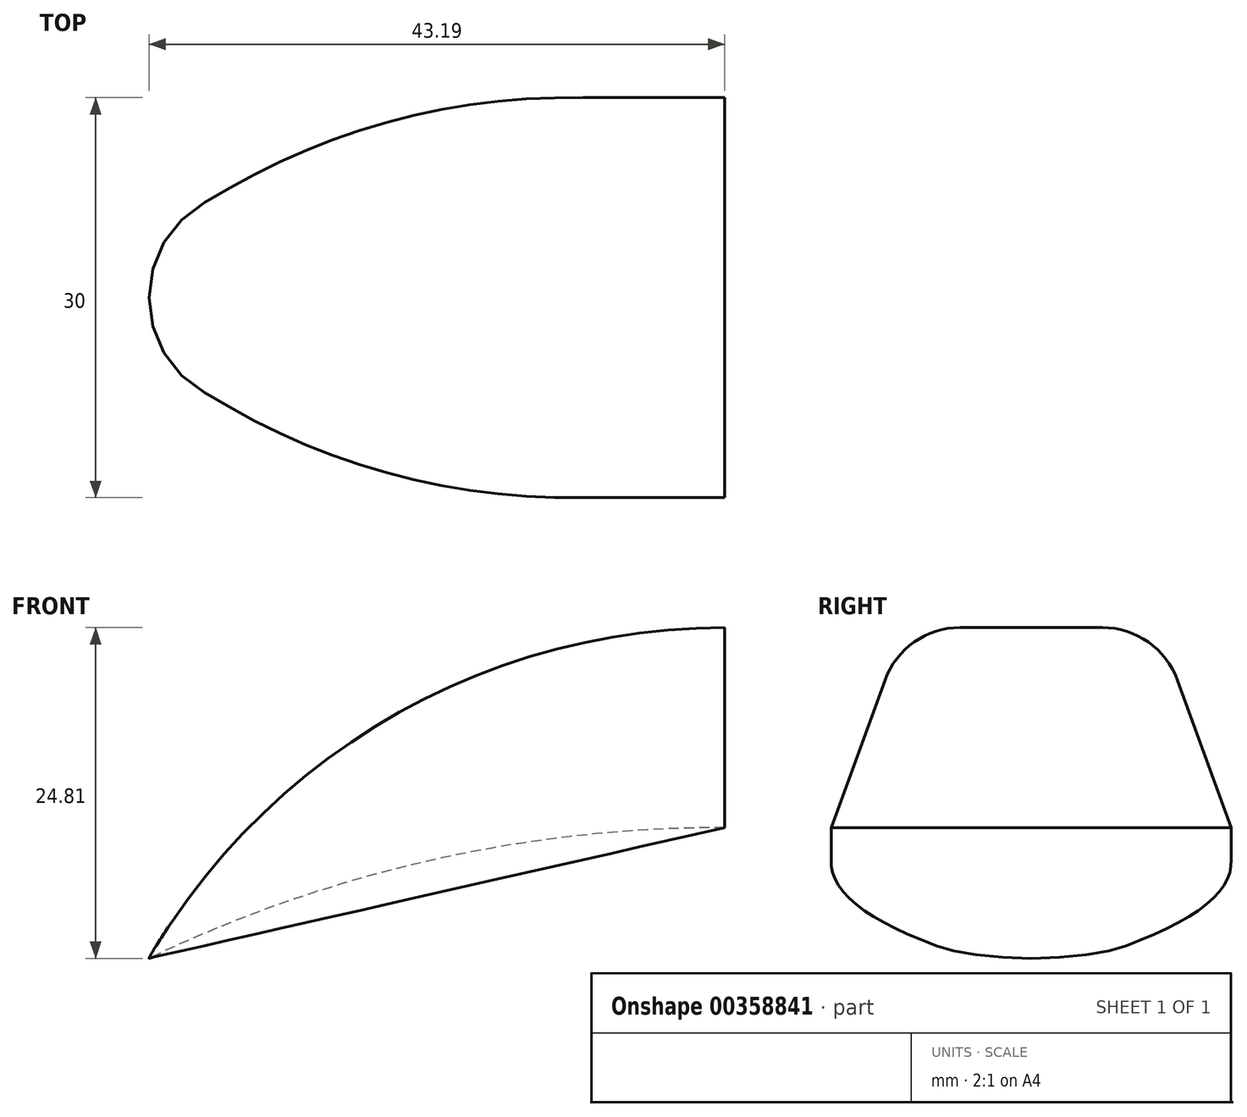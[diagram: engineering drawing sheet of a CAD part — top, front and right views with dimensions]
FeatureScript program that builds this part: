
annotation { "Feature Type Name" : "Feature", "Feature Type Description" : "" }
export const myFeature = defineFeature(function(context is Context, id is Id, definition is map)
    precondition{}
    {
        {
            var Q0;
            Q0=qCreatedBy(makeId("Right.planeOp"),FACE);
            var sketch = newSketch(context, id + "F0", { "sketchPlane" : qUnion([Q0])});
            skLineSegment(sketch, "E0", {"start": v(10.98, 11.05) * mm, "end": v(15, 0) * mm});
            skLineSegment(sketch, "E1.MirrorCS", {"start": v(-10.98, 11.05) * mm, "end": v(-15, 0) * mm});
            skLineSegment(sketch, "E2", {"start": v(-5.34, 15) * mm, "end": v(5.34, 15) * mm});
            skPoint(sketch, "E3.visualSharp", {"position": v(-9.54, 15) * mm});
            skArc(sketch, "E3.filletArc", {"start": v(-5.34, 15) * mm, "mid": v(-8.78, 13.91) * mm, "end": v(-10.98, 11.05) * mm});
            skPoint(sketch, "E4.visualSharp", {"position": v(9.54, 15) * mm});
            skArc(sketch, "E4.filletArc", {"start": v(10.98, 11.05) * mm, "mid": v(8.78, 13.91) * mm, "end": v(5.34, 15) * mm});
            skLineSegment(sketch, "E5", {"start": v(15, 0) * mm, "end": v(-15, 0) * mm});
            skSolve(sketch);
        }
        {
            var Q0;
            Q0=qCreatedBy(makeId("Front.planeOp"),FACE);
            var sketch = newSketch(context, id + "F1", { "sketchPlane" : qUnion([Q0])});
            skArc(sketch, "E6", {"start": v(0, 15) * mm, "mid": v(-24.9, 8.36) * mm, "end": v(-43.19, -9.8) * mm});
            skArc(sketch, "E7", {"start": v(0, 0) * mm, "mid": v(-22.14, -2.48) * mm, "end": v(-43.19, -9.8) * mm});
            skLineSegment(sketch, "E8", {"start": v(0, 43.12) * mm, "end": v(0, -53.25) * mm, "construction": true});
            skLineSegment(sketch, "E9", {"start": v(0, 0) * mm, "end": v(-43.19, -9.8) * mm});
            skSolve(sketch);
        }
        {
            var Q0;
            Q0=qCreatedBy(makeId("Top.planeOp"),FACE);
            var sketch = newSketch(context, id + "F2", { "sketchPlane" : qUnion([Q0])});
            skArc(sketch, "E10", {"start": v(-39.62, 6.66) * mm, "mid": v(-42.24, 3.78) * mm, "end": v(-43.19, 0) * mm});
            skLineSegment(sketch, "E11", {"start": v(0, 15) * mm, "end": v(-12, 15) * mm});
            skArc(sketch, "E12", {"start": v(-12, 15) * mm, "mid": v(-26.42, 12.87) * mm, "end": v(-39.62, 6.66) * mm});
            skLineSegment(sketch, "E13", {"start": v(15.58, 0) * mm, "end": v(-62.95, 0) * mm, "construction": true});
            skLineSegment(sketch, "E14.MirrorCS", {"start": v(0, -15) * mm, "end": v(-12, -15) * mm});
            skArc(sketch, "E15.MirrorCS", {"start": v(-12, -15) * mm, "mid": v(-26.42, -12.87) * mm, "end": v(-39.62, -6.66) * mm});
            skArc(sketch, "E16.MirrorCS", {"start": v(-39.62, -6.66) * mm, "mid": v(-42.24, -3.78) * mm, "end": v(-43.19, 0) * mm});
            skSolve(sketch);
        }
        {
            var Q0;
            Q0=sQuery(id+"F2.wireOp",VERTEX,"E11.start");
            var Q1;
            Q1=sQuery(id+"F1.wireOp",VERTEX,"E9.start");
            var Q2;
            Q2=sQuery(id+"F1.wireOp",VERTEX,"E6.end");
            cPlane(context, id + "F3", {"entities" : qUnion([Q0, Q1, Q2]), "cplaneType" : CPlaneType.THREE_POINT, "offset" : 25 * mm, "width" : 150 * mm, "height" : 150 * mm});
        }
        {
            var Q0;
            Q0=qCreatedBy(id+"F3.planeOp",FACE);
            var sketch = newSketch(context, id + "F4", { "sketchPlane" : qUnion([Q0])});
            skArc(sketch, "E17", {"start": v(-40.55, 6.77) * mm, "mid": v(-43.3, 3.87) * mm, "end": v(-44.29, 0) * mm});
            skLineSegment(sketch, "E18", {"start": v(0, 15) * mm, "end": v(-12, 15) * mm});
            skArc(sketch, "E19", {"start": v(-12, 15) * mm, "mid": v(-26.85, 12.9) * mm, "end": v(-40.55, 6.77) * mm});
            skLineSegment(sketch, "E20", {"start": v(15.08, 0) * mm, "end": v(-61.73, 0) * mm, "construction": true});
            skSolve(sketch);
        }
        {
            var Q0;
            Q0=qCreatedBy(id+"F3.planeOp",FACE);
            var sketch = newSketch(context, id + "F5", { "sketchPlane" : qUnion([Q0])});
            skLineSegment(sketch, "E21.MirrorCS", {"start": v(0, -15) * mm, "end": v(-12, -15) * mm});
            skArc(sketch, "E22.MirrorCS", {"start": v(-12, -15) * mm, "mid": v(-26.85, -12.9) * mm, "end": v(-40.55, -6.77) * mm});
            skArc(sketch, "E23.MirrorCS", {"start": v(-40.55, -6.77) * mm, "mid": v(-43.3, -3.87) * mm, "end": v(-44.29, 0) * mm});
            skSolve(sketch);
        }
        {
            var Q0;
            Q0=makeQuery(id+"F0.imprint","IMPRINT",FACE,{"disambiguationData":[TD([[makeQuery(id+"F0.imprint","IMPRINT",EDGE,{"derivedFrom":sQuery(id+"F0.wireOp",EDGE,"E0")}),-1.0]])]});
            var Q1;
            Q1=sQuery(id+"F1.wireOp",VERTEX,"E7.end");
            var Q2;
            Q2 = qConstructionFilter(qBodyType(qCreatedBy(id + "F4" ,EDGE), BodyType.WIRE), ConstructionObject.NO);
            var Q3;
            Q3=sQuery(id+"F1.wireOp",EDGE,"E6");
            var Q4;
            Q4 = qConstructionFilter(qBodyType(qCreatedBy(id + "F5" ,EDGE), BodyType.WIRE), ConstructionObject.NO);
            var Q5;
            Q5=sQuery(id+"F1.wireOp",EDGE,"E7");
            loft(context, id + "F6", {"addGuides" : true, "sheetProfilesArray" : [{ "sheetProfileEntities" : qUnion([Q0]) }, { "sheetProfileEntities" : qUnion([Q1]) }], "guidesArray" : [{ "guideEntities" : qUnion([Q2]), "guideDerivativeType" : LoftGuideDerivativeType.DEFAULT, "guideDerivativeMagnitude" : 1 }, { "guideEntities" : qUnion([Q3]), "guideDerivativeType" : LoftGuideDerivativeType.DEFAULT, "guideDerivativeMagnitude" : 1 }, { "guideEntities" : qUnion([Q4]), "guideDerivativeType" : LoftGuideDerivativeType.DEFAULT, "guideDerivativeMagnitude" : 1 }, { "guideEntities" : qUnion([Q5]), "guideDerivativeType" : LoftGuideDerivativeType.DEFAULT, "guideDerivativeMagnitude" : 1 }]});
        }
    });
